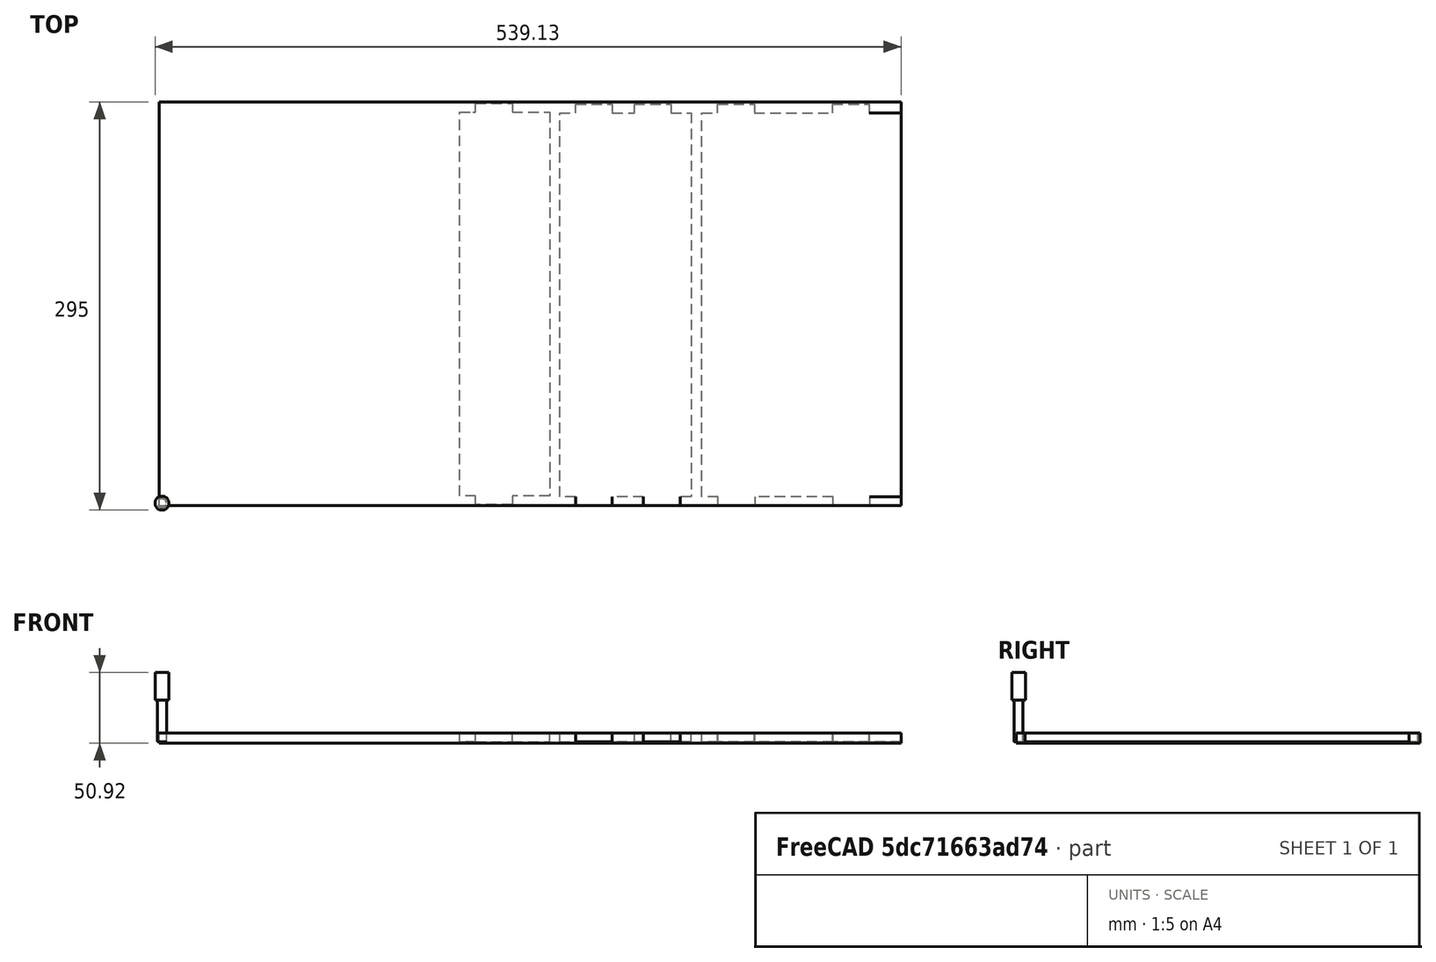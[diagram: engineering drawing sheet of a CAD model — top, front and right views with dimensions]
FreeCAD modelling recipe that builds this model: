
FCSTD DOCUMENT  (FreeCAD 0.19RUnknown)
Label: Stand3
License: All rights reserved
LicenseURL: http://en.wikipedia.org/wiki/All_rights_reserved
objects: Part::FeaturePython×7, Path::FeaturePython×5, Sketcher::SketchObject×4, PartDesign::Pad×4, PartDesign::Body×4, App::DocumentObjectGroup×2, PartDesign::Fillet×1, Spreadsheet::Sheet×1, Part::Mirroring×1, Mesh::FeaturePython×1, App::FeaturePython×1, Path::FeatureCompoundPython×1
note: 29 computed .brp shape members not serialized (recipe doc carries the construction recipe); baked Part::Feature solids carry a one-line shape summary decoded from their .brp

FEATURE [Sketcher::SketchObject] Sketch
  FullyConstrained = true
  MapMode = 5
  Support = -> [XY_Plane]
  expr: .Constraints.LowerSlotGap = <<Spreadsheet>>.TongueGapLower
  expr: Constraints[67] = <<Spreadsheet>>.Tool
  expr: Constraints[94] = <<Spreadsheet>>.SlotCentre
  expr: Constraints[83] = <<Spreadsheet>>.TongueToBack
  expr: Constraints[81] = <<Spreadsheet>>.Tool
  expr: Constraints[92] = <<Spreadsheet>>.Tool
  expr: Constraints[72] = <<Spreadsheet>>.TongueToBack
  expr: Constraints[91] = <<Spreadsheet>>.SlotSize
  expr: Constraints[71] = <<Spreadsheet>>.SlotSize
  expr: Constraints[53] = <<Spreadsheet>>.Tool
  expr: Constraints[68] = <<Spreadsheet>>.Tool
  expr: Constraints[82] = <<Spreadsheet>>.SlotSize
  expr: Constraints[52] = <<Spreadsheet>>.SlotSize
  expr: Constraints[27] = <<Spreadsheet>>.Top
  expr: Constraints[70] = <<Spreadsheet>>.SlotSize
  expr: Constraints[55] = <<Spreadsheet>>.TongueToBack
  expr: Constraints[29] = <<Spreadsheet>>.Bottom
  expr: .Constraints.MidSlotGap = <<Spreadsheet>>.TongueGapMid
  expr: Constraints[26] = <<Spreadsheet>>.Height
  expr: Constraints[107] = <<Spreadsheet>>.TongueToBack
  sketch-geometry (40):
    g0: LineSegment StartX=0 StartY=290 StartZ=0 EndX=50 EndY=290 EndZ=0
    g1: LineSegment StartX=150 StartY=0 StartZ=0 EndX=120 EndY=0 EndZ=0
    g2: LineSegment StartX=0 StartY=0 StartZ=0 EndX=0 EndY=290 EndZ=0
    g3: LineSegment StartX=50 StartY=290 StartZ=0 EndX=150 EndY=0 EndZ=0
    g4: LineSegment StartX=15 StartY=210 StartZ=0 EndX=15 EndY=130 EndZ=0
    g5: LineSegment StartX=15 StartY=130 StartZ=0 EndX=89.3057 EndY=130 EndZ=0
    g6: LineSegment StartX=89.3057 StartY=130 StartZ=0 EndX=61.7195 EndY=210 EndZ=0
    g7: LineSegment StartX=61.7195 StartY=210 StartZ=0 EndX=15 EndY=210 EndZ=0
    g8: LineSegment StartX=15 StartY=110 StartZ=0 EndX=15 EndY=33.2 EndZ=0
    g9: LineSegment StartX=15 StartY=33.2 StartZ=0 EndX=122.685 EndY=33.2 EndZ=0
    g10: LineSegment StartX=122.685 StartY=33.2 StartZ=0 EndX=96.2022 EndY=110 EndZ=0
    g11: LineSegment StartX=96.2022 StartY=110 StartZ=0 EndX=15 EndY=110 EndZ=0
    g12: LineSegment StartX=120 StartY=0 StartZ=0 EndX=120 EndY=13.2 EndZ=0
    g13: LineSegment StartX=120 StartY=13.2 StartZ=0 EndX=30 EndY=13.2 EndZ=0
    g14: LineSegment StartX=30 StartY=13.2 StartZ=0 EndX=30 EndY=0 EndZ=0
    g15: LineSegment StartX=30 StartY=0 StartZ=0 EndX=0 EndY=0 EndZ=0
    g16: ArcOfCircle CenterX=18 CenterY=220 CenterZ=0 NormalX=0 NormalY=0 NormalZ=1 AngleXU=0 Radius=3.25 StartAngle=1.5708 EndAngle=4.71239
    g17: ArcOfCircle CenterX=38 CenterY=220 CenterZ=0 NormalX=0 NormalY=0 NormalZ=1 AngleXU=0 Radius=3.25 StartAngle=4.71239 EndAngle=7.85398
    g18: LineSegment StartX=18 StartY=216.75 StartZ=0 EndX=38 EndY=216.75 EndZ=0
    g19: LineSegment StartX=38 StartY=223.25 StartZ=0 EndX=18 EndY=223.25 EndZ=0
    g20: ArcOfCircle CenterX=60.5 CenterY=120 CenterZ=0 NormalX=0 NormalY=0 NormalZ=1 AngleXU=0 Radius=3.25 StartAngle=1.5708 EndAngle=4.71239
    g21: ArcOfCircle CenterX=80.5 CenterY=120 CenterZ=0 NormalX=0 NormalY=0 NormalZ=1 AngleXU=0 Radius=3.25 StartAngle=4.71239 EndAngle=7.85398
    g22: LineSegment StartX=60.5 StartY=116.75 StartZ=0 EndX=80.5 EndY=116.75 EndZ=0
    g23: LineSegment StartX=80.5 StartY=123.25 StartZ=0 EndX=60.5 EndY=123.25 EndZ=0
    g24: ArcOfCircle CenterX=18 CenterY=120 CenterZ=0 NormalX=0 NormalY=0 NormalZ=1 AngleXU=0 Radius=3.25 StartAngle=1.5708 EndAngle=4.71239
    g25: ArcOfCircle CenterX=38 CenterY=120 CenterZ=0 NormalX=0 NormalY=0 NormalZ=1 AngleXU=0 Radius=3.25 StartAngle=4.71239 EndAngle=7.85398
    g26: LineSegment StartX=18 StartY=116.75 StartZ=0 EndX=38 EndY=116.75 EndZ=0
    g27: LineSegment StartX=38 StartY=123.25 StartZ=0 EndX=18 EndY=123.25 EndZ=0
    g28: ArcOfCircle CenterX=18 CenterY=23.2 CenterZ=0 NormalX=0 NormalY=0 NormalZ=1 AngleXU=0 Radius=3.25 StartAngle=1.5708 EndAngle=4.71239
    g29: ArcOfCircle CenterX=38 CenterY=23.2 CenterZ=0 NormalX=0 NormalY=0 NormalZ=1 AngleXU=0 Radius=3.25 StartAngle=4.71239 EndAngle=7.85398
    g30: LineSegment StartX=18 StartY=19.95 StartZ=0 EndX=38 EndY=19.95 EndZ=0
    g31: LineSegment StartX=38 StartY=26.45 StartZ=0 EndX=18 EndY=26.45 EndZ=0
    g32: ArcOfCircle CenterX=101 CenterY=23.2 CenterZ=0 NormalX=0 NormalY=0 NormalZ=1 AngleXU=0 Radius=3.25 StartAngle=1.5708 EndAngle=4.71239
    g33: ArcOfCircle CenterX=121 CenterY=23.2 CenterZ=0 NormalX=0 NormalY=0 NormalZ=1 AngleXU=0 Radius=3.25 StartAngle=4.71239 EndAngle=7.85398
    g34: LineSegment StartX=101 StartY=19.95 StartZ=0 EndX=121 EndY=19.95 EndZ=0
    g35: LineSegment StartX=121 StartY=26.45 StartZ=0 EndX=101 EndY=26.45 EndZ=0
    g36: LineSegment StartX=18 StartY=280 StartZ=0 EndX=18 EndY=230 EndZ=0
    g37: LineSegment StartX=18 StartY=230 StartZ=0 EndX=54.8229 EndY=230 EndZ=0
    g38: LineSegment StartX=54.8229 StartY=230 StartZ=0 EndX=37.5815 EndY=280 EndZ=0
    g39: LineSegment StartX=37.5815 StartY=280 StartZ=0 EndX=18 EndY=280 EndZ=0
  constraints (109):
    c: Coincident(g15,g2)
    c: Coincident(g2,g0)
    c: Horizontal(g0)
    c: Horizontal(g1)
    c: Vertical(g2)
    c: Vertical(g4)
    c: Coincident(g4,g5)
    c: Horizontal(g5)
    c: Coincident(g5,g6)
    c: Coincident(g6,g7)
    c: Coincident(g7,g4)
    c: Vertical(g8)
    c: Coincident(g8,g9)
    c: Coincident(g9,g10)
    c: Coincident(g10,g11)
    c: Coincident(g11,g8)
    c: Horizontal(g11)
    c: Coincident(g12,g13)
    c: Coincident(g13,g14)
    c: Horizontal(g13)
    c: Vertical(g12)
    c: Vertical(g14)
    c: Coincident(g15,g-1)
    c: Coincident(g0,g3)
    c: Parallel(g3,g10)
    c: Parallel(g3,g6)
    c: DistanceY(g2,g2) = 290
    c: DistanceX(g0,g0) = 50
    c: Coincident(g3,g1)
    c: DistanceX(g2,g1) = 150
    c: DistanceX(g15,g15) = 30
    c: DistanceX(g1,g1) = 30
    c: Coincident(g12,g1)
    c: Parallel(g13,g9)
    c: Parallel(g5,g7)
    c: Coincident(g14,g15)
    c: DistanceY(g14,g13) = 13.2
    c: DistanceY(g13,g8) = 20
    c: DistanceY(g8,g4) = 20
    c: DistanceY(g4,g0) = 80
    c: DistanceX(g2,g8) = 15
    c: DistanceX(g2,g4) = 15
    c: Horizontal(g15)
    c: Distance(g5,g3) = 15
    c: Distance(g10,g3) = 15
    c: DistanceY(g1,g2) = 0
    c: Tangent(g16,g18) = -1.5708
    c: Tangent(g18,g17) = -1.5708
    c: Tangent(g17,g19) = -1.5708
    c: Tangent(g19,g16) = -1.5708
    c: Equal(g16,g17)
    c: Horizontal(g18)
    c: DistanceX(g16,g17) = 20
    c: Diameter(g17) = 6.5
    c: DistanceY(g4,g16) = 10
    c: DistanceX(g0,g16) = 18
    c: Tangent(g20,g22) = -1.5708
    c: Tangent(g22,g21) = -1.5708
    c: Tangent(g21,g23) = -1.5708
    c: Tangent(g23,g20) = -1.5708
    c: Equal(g20,g21)
    c: Horizontal(g22)
    c: Tangent(g24,g26) = -1.5708
    c: Tangent(g26,g25) = -1.5708
    c: Tangent(g25,g27) = -1.5708
    c: Tangent(g27,g24) = -1.5708
    c: Equal(g24,g25)
    c: Diameter(g21) = 6.5
    c: Diameter(g24) = 6.5
    c: Parallel(g27,g5)
    c: DistanceX(g20,g21) = 20
    c: DistanceX(g24,g25) = 20
    c: DistanceX(g2,g24) = 18
    c: DistanceY(g8,g24) = 10
    c: DistanceY(g10,g21) = 10
    c: Tangent(g28,g30) = -1.5708
    c: Tangent(g30,g29) = -1.5708
    c: Tangent(g29,g31) = -1.5708
    c: Tangent(g31,g28) = -1.5708
    c: Equal(g28,g29)
    c: Horizontal(g30)
    c: Diameter(g29) = 6.5
    c: DistanceX(g28,g29) = 20
    c: DistanceX(g2,g28) = 18
    c: DistanceY(g13,g28) = 10
    c: Tangent(g32,g34) = -1.5708
    c: Tangent(g34,g33) = -1.5708
    c: Tangent(g33,g35) = -1.5708
    c: Tangent(g35,g32) = -1.5708
    c: Equal(g32,g33)
    c: Horizontal(g34)
    c: DistanceX(g32,g33) = 20
    c: Diameter(g33) = 6.5
    c: DistanceY(g12,g33) = 10
    c: DistanceY(g2,g24) = 120
    c: DistanceX(g25,g20) = 22.5  'MidSlotGap'
    c: DistanceX(g29,g32) = 63  'LowerSlotGap'
    c: Vertical(g36)
    c: Coincident(g36,g37)
    c: Horizontal(g37)
    c: Coincident(g37,g38)
    c: Coincident(g38,g39)
    c: Coincident(g39,g36)
    c: Horizontal(g39)
    c: DistanceY(g16,g36) = 10
    c: DistanceY(g36,g0) = 10
    c: Parallel(g38,g3)
    c: DistanceX(g0,g36) = 18
    c: Distance(g37,g3) = 15
FEATURE [PartDesign::Pad] Pad
  Direction = (0,0,1)
  Length = 6.25
  Length2 = 100
  Profile = -> Sketch
  Type = 0
  expr: Length = <<Spreadsheet>>.Thickness
FEATURE [PartDesign::Fillet] Fillet
  Base = -> Pad [Edge20,Edge2,Edge1,Edge5,Edge8,Edge17,Edge44,Edge37,Edge32,Edge25,Edge38,Edge26,Edge29,Edge41,Edge14,Edge11,Edge49,Edge50,Edge56,Edge53]
  BaseFeature = -> Pad
  Radius = 6.5
  SupportTransform = false
  expr: Radius = <<Spreadsheet>>.Tool
FEATURE [PartDesign::Body] Body
  Group = -> [Sketch,Pad,Fillet]
  Origin = -> Origin
  Placement = pos=(-2,0,0) rot=(0,0,1;0rad)
  Tip = -> Fillet
FEATURE [Spreadsheet::Sheet] Spreadsheet
  cells = A2=Material Thickness; B2(Thickness)=6.25; A3=Tool Size; B3(Tool)=6.5; A5=Height; B5(Height)=290; A6=Bottom Width; B6(Bottom)=150; A7=Top Width; B7(Top)=50; A8=SlotSize; B8(SlotSize)=20; A9=TongueSize; B9(TongueSize)==B8 + B3; A10=Tongue to back; B10(TongueToBack)=18; A11=Centre; B11(SlotCentre)=120; A12=Mid Tongue Gap; B12(TongueGapMid)=22.5; A13=Lower Tongue Gap; B13(TongueGapLower)=63; A15=TopShelf; B15(ShelfTop)=65; A16=MidShelf; B16(ShelfMid)==(B6 + B7) / 2 - 5; A17=Bottom Shelf; B17(ShelfBottom)==B6 - 6; A18=Shelf Width; B18(ShelfWidth)==B5 - B2 * 2
FEATURE [Part::Mirroring] mirror  label="Body (mirrored) "
  Base = (159.181,124.226,5.79083)
  Normal = (-0.999887,-0.00161748,0.0149187)
  Placement = pos=(-113.202,287.893,10.586) rot=(0.99989,0.002927,-0.014571;3.14394rad)
  Source = -> Body
FEATURE [Sketcher::SketchObject] Sketch001
  FullyConstrained = false
  MapMode = 5
  Support = -> [XY_Plane001]
  expr: Constraints[34] = <<Spreadsheet>>.ShelfWidth
  expr: Constraints[30] = <<Spreadsheet>>.TongueToBack - <<Spreadsheet>>.Tool
  expr: Constraints[9] = <<Spreadsheet>>.ShelfWidth
  expr: Constraints[27] = <<Spreadsheet>>.Thickness
  expr: Constraints[29] = <<Spreadsheet>>.TongueToBack - <<Spreadsheet>>.Tool
  expr: Constraints[26] = <<Spreadsheet>>.TongueSize
  expr: Constraints[8] = <<Spreadsheet>>.ShelfTop
  expr: Constraints[16] = <<Spreadsheet>>.Thickness
  expr: Constraints[15] = <<Spreadsheet>>.TongueSize
  sketch-geometry (13):
    g0: LineSegment StartX=222.154 StartY=283.723 StartZ=0 EndX=231.81 EndY=283.723 EndZ=0
    g1: LineSegment StartX=287.154 StartY=283.75 StartZ=0 EndX=287.154 EndY=6.25 EndZ=0
    g2: LineSegment StartX=287.154 StartY=6.25 StartZ=0 EndX=260.154 EndY=6.25 EndZ=0
    g3: LineSegment StartX=222.154 StartY=6.22299 StartZ=0 EndX=222.154 EndY=283.723 EndZ=0
    g4: LineSegment StartX=260.154 StartY=6.25 StartZ=0 EndX=260.154 EndY=0 EndZ=0
    g5: LineSegment StartX=260.154 StartY=0 StartZ=0 EndX=233.654 EndY=0 EndZ=0
    g6: LineSegment StartX=233.654 StartY=0 StartZ=0 EndX=233.654 EndY=6.22299 EndZ=0
    g7: LineSegment StartX=233.654 StartY=6.22299 StartZ=0 EndX=222.154 EndY=6.22299 EndZ=0
    g8: LineSegment StartX=233.654 StartY=290 StartZ=0 EndX=260.154 EndY=290 EndZ=0
    g9: LineSegment StartX=260.154 StartY=290 StartZ=0 EndX=260.154 EndY=283.75 EndZ=0
    g10: LineSegment StartX=231.81 StartY=283.723 StartZ=0 EndX=233.654 EndY=283.723 EndZ=0
    g11: LineSegment StartX=233.654 StartY=283.723 StartZ=0 EndX=233.654 EndY=290 EndZ=0
    g12: LineSegment StartX=260.154 StartY=283.75 StartZ=0 EndX=287.154 EndY=283.75 EndZ=0
  constraints (36):
    c: Coincident(g12,g1)
    c: Coincident(g1,g2)
    c: Coincident(g7,g3)
    c: Coincident(g3,g0)
    c: Horizontal(g0)
    c: Horizontal(g2)
    c: Vertical(g1)
    c: Vertical(g3)
    c: DistanceX(g0,g12) = 65
    c: DistanceY(g3,g3) = 277.5
    c: Coincident(g4,g5)
    c: Coincident(g5,g6)
    c: Horizontal(g5)
    c: Vertical(g4)
    c: Vertical(g6)
    c: DistanceX(g5,g5) = 26.5
    c: DistanceY(g4,g4) = 6.25
    c: DistanceY(g-1,g5) = 0
    c: Parallel(g5,g7)
    c: Coincident(g8,g9)
    c: Coincident(g10,g11)
    c: Coincident(g11,g8)
    c: Horizontal(g8)
    c: Horizontal(g10)
    c: Vertical(g9)
    c: Vertical(g11)
    c: DistanceX(g8,g8) = 26.5
    c: DistanceY(g9,g9) = 6.25
    c: PointOnObject(g10,g0)
    c: DistanceX(g0,g8) = 11.5
    c: DistanceX(g3,g5) = 11.5
    c: Coincident(g7,g6)
    c: Coincident(g12,g9)
    c: Coincident(g2,g4)
    c: DistanceY(g1,g1) = 277.5
    c: Parallel(g12,g8)
FEATURE [PartDesign::Pad] Pad001
  Direction = (0,0,1)
  Length = 6.25
  Length2 = 10
  Profile = -> Sketch001
  Type = 0
  expr: Length = <<Spreadsheet>>.Thickness
FEATURE [PartDesign::Body] Body001  label="TopShelf"
  Group = -> [Sketch001,Pad001]
  Origin = -> Origin001
  Placement = pos=(-7,-1,0) rot=(0,0,1;0rad)
  Tip = -> Pad001
FEATURE [Sketcher::SketchObject] Sketch002
  FullyConstrained = false
  MapMode = 5
  Support = -> [XY_Plane002]
  expr: Constraints[9] = <<Spreadsheet>>.ShelfMid
  expr: Constraints[57] = <<Spreadsheet>>.ShelfWidth
  expr: Constraints[55] = <<Spreadsheet>>.Thickness
  expr: Constraints[54] = <<Spreadsheet>>.Thickness
  expr: Constraints[8] = <<Spreadsheet>>.ShelfWidth
  expr: Constraints[56] = <<Spreadsheet>>.Thickness
  expr: Constraints[48] = <<Spreadsheet>>.Thickness
  expr: Constraints[47] = <<Spreadsheet>>.Thickness
  expr: Constraints[46] = <<Spreadsheet>>.Thickness
  expr: Constraints[42] = <<Spreadsheet>>.TongueGapMid
  expr: Constraints[37] = <<Spreadsheet>>.TongueToBack - <<Spreadsheet>>.Tool
  expr: Constraints[43] = <<Spreadsheet>>.TongueSize
  expr: Constraints[36] = <<Spreadsheet>>.TongueSize
  expr: Constraints[58] = <<Spreadsheet>>.Thickness
  expr: Constraints[49] = <<Spreadsheet>>.Thickness
  expr: Constraints[33] = <<Spreadsheet>>.TongueSize
  expr: Constraints[38] = <<Spreadsheet>>.TongueSize
  expr: Constraints[32] = <<Spreadsheet>>.TongueGapMid - <<Spreadsheet>>.Tool
  expr: Constraints[31] = <<Spreadsheet>>.TongueToBack - <<Spreadsheet>>.Tool
  sketch-geometry (20):
    g0: LineSegment StartX=280.428 StartY=276.137 StartZ=0 EndX=291.928 EndY=276.137 EndZ=0
    g1: LineSegment StartX=375.428 StartY=276.137 StartZ=0 EndX=375.428 EndY=-1.36323 EndZ=0
    g2: LineSegment StartX=375.428 StartY=-1.36323 StartZ=0 EndX=367.428 EndY=-1.36323 EndZ=0
    g3: LineSegment StartX=280.428 StartY=-1.36323 StartZ=0 EndX=280.428 EndY=276.137 EndZ=0
    g4: LineSegment StartX=291.928 StartY=282.387 StartZ=0 EndX=318.428 EndY=282.387 EndZ=0
    g5: LineSegment StartX=318.428 StartY=282.387 StartZ=0 EndX=318.428 EndY=276.137 EndZ=0
    g6: LineSegment StartX=291.928 StartY=276.137 StartZ=0 EndX=291.928 EndY=282.387 EndZ=0
    g7: LineSegment StartX=334.428 StartY=282.387 StartZ=0 EndX=360.928 EndY=282.387 EndZ=0
    g8: LineSegment StartX=360.928 StartY=282.387 StartZ=0 EndX=360.928 EndY=276.137 EndZ=0
    g9: LineSegment StartX=334.428 StartY=276.137 StartZ=0 EndX=334.428 EndY=282.387 EndZ=0
    g10: LineSegment StartX=318.428 StartY=-1.36323 StartZ=0 EndX=318.428 EndY=-7.61323 EndZ=0
    g11: LineSegment StartX=318.428 StartY=-7.61323 StartZ=0 EndX=291.928 EndY=-7.61323 EndZ=0
    g12: LineSegment StartX=291.928 StartY=-7.61323 StartZ=0 EndX=291.928 EndY=-1.36323 EndZ=0
    g13: LineSegment StartX=367.428 StartY=-1.36323 StartZ=0 EndX=367.428 EndY=-7.61323 EndZ=0
    g14: LineSegment StartX=367.428 StartY=-7.61323 StartZ=0 EndX=340.928 EndY=-7.61323 EndZ=0
    g15: LineSegment StartX=340.928 StartY=-7.61323 StartZ=0 EndX=340.928 EndY=-1.36323 EndZ=0
    g16: LineSegment StartX=318.428 StartY=276.137 StartZ=0 EndX=334.428 EndY=276.137 EndZ=0
    g17: LineSegment StartX=360.928 StartY=276.137 StartZ=0 EndX=375.428 EndY=276.137 EndZ=0
    g18: LineSegment StartX=291.928 StartY=-1.36323 StartZ=0 EndX=280.428 EndY=-1.36323 EndZ=0
    g19: LineSegment StartX=340.928 StartY=-1.36323 StartZ=0 EndX=318.428 EndY=-1.36323 EndZ=0
  constraints (59):
    c: Coincident(g17,g1)
    c: Coincident(g1,g2)
    c: Coincident(g18,g3)
    c: Coincident(g3,g0)
    c: Horizontal(g0)
    c: Horizontal(g2)
    c: Vertical(g1)
    c: Vertical(g3)
    c: DistanceY(g1,g1) = 277.5
    c: DistanceX(g0,g17) = 95
    c: Coincident(g4,g5)
    c: Coincident(g6,g4)
    c: Horizontal(g4)
    c: Vertical(g5)
    c: Vertical(g6)
    c: Coincident(g7,g8)
    c: Coincident(g9,g7)
    c: Horizontal(g7)
    c: Vertical(g8)
    c: Vertical(g9)
    c: PointOnObject(g8,g0)
    c: Coincident(g10,g11)
    c: Coincident(g11,g12)
    c: Horizontal(g11)
    c: Vertical(g10)
    c: Vertical(g12)
    c: Coincident(g13,g14)
    c: Coincident(g14,g15)
    c: Horizontal(g14)
    c: Vertical(g13)
    c: Vertical(g15)
    c: DistanceX(g0,g4) = 11.5
    c: DistanceX(g4,g7) = 16
    c: DistanceX(g4,g4) = 26.5
    c: Coincident(g16,g5)
    c: PointOnObject(g16,g9)
    c: DistanceX(g7,g7) = 26.5
    c: DistanceX(g3,g11) = 11.5
    c: DistanceX(g11,g11) = 26.5
    c: Coincident(g18,g12)
    c: Coincident(g10,g19)
    c: Coincident(g19,g15)
    c: DistanceX(g19,g19) = 22.5
    c: DistanceX(g14,g14) = 26.5
    c: Coincident(g0,g6)
    c: Coincident(g17,g8)
    c: DistanceY(g1,g7) = 6.25
    c: DistanceY(g9,g9) = 6.25
    c: DistanceY(g5,g5) = 6.25
    c: DistanceY(g6,g6) = 6.25
    c: Parallel(g16,g4)
    c: Parallel(g18,g11)
    c: Parallel(g19,g11)
    c: Coincident(g2,g13)
    c: DistanceY(g12,g12) = 6.25
    c: DistanceY(g15,g15) = 6.25
    c: DistanceY(g13,g13) = 6.25
    c: DistanceY(g3,g3) = 277.5
    c: DistanceY(g10,g10) = 6.25
FEATURE [PartDesign::Pad] Pad002
  Direction = (0,0,1)
  Length = 6.25
  Length2 = 10
  Profile = -> Sketch002
  Type = 0
  expr: Length = <<Spreadsheet>>.Thickness
FEATURE [PartDesign::Body] Body002  label="MidShelf"
  Group = -> [Sketch002,Pad002]
  Origin = -> Origin002
  Placement = pos=(7,6,0) rot=(0,0,1;0rad)
  Tip = -> Pad002
FEATURE [Sketcher::SketchObject] Sketch003
  FullyConstrained = false
  MapMode = 5
  Support = -> [XY_Plane003]
  expr: Constraints[57] = <<Spreadsheet>>.Thickness
  expr: Constraints[55] = <<Spreadsheet>>.ShelfWidth
  expr: Constraints[54] = <<Spreadsheet>>.TongueToBack - <<Spreadsheet>>.Thickness
  expr: Constraints[53] = <<Spreadsheet>>.TongueGapLower - <<Spreadsheet>>.Tool
  expr: Constraints[51] = <<Spreadsheet>>.TongueSize
  expr: Constraints[4] = <<Spreadsheet>>.ShelfBottom
  expr: Constraints[46] = <<Spreadsheet>>.Thickness
  expr: Constraints[45] = <<Spreadsheet>>.Thickness
  expr: Constraints[49] = <<Spreadsheet>>.Thickness
  expr: Constraints[56] = <<Spreadsheet>>.Thickness
  expr: Constraints[44] = <<Spreadsheet>>.Thickness
  expr: Constraints[52] = <<Spreadsheet>>.TongueSize
  expr: Constraints[48] = <<Spreadsheet>>.ShelfWidth
  expr: Constraints[37] = <<Spreadsheet>>.TongueToBack - <<Spreadsheet>>.Tool
  expr: Constraints[35] = <<Spreadsheet>>.TongueSize
  expr: Constraints[34] = <<Spreadsheet>>.TongueSize
  expr: Constraints[36] = <<Spreadsheet>>.TongueGapLower - <<Spreadsheet>>.Tool
  expr: Constraints[50] = <<Spreadsheet>>.Thickness
  sketch-geometry (20):
    g0: LineSegment StartX=533.13 StartY=286.184 StartZ=0 EndX=533.13 EndY=8.68426 EndZ=0
    g1: LineSegment StartX=533.13 StartY=8.68426 StartZ=0 EndX=510.38 EndY=8.68426 EndZ=0
    g2: LineSegment StartX=389.13 StartY=8.68426 StartZ=0 EndX=389.13 EndY=286.184 EndZ=0
    g3: LineSegment StartX=400.63 StartY=292.434 StartZ=0 EndX=427.13 EndY=292.434 EndZ=0
    g4: LineSegment StartX=427.13 StartY=292.434 StartZ=0 EndX=427.13 EndY=286.184 EndZ=0
    g5: LineSegment StartX=400.63 StartY=286.184 StartZ=0 EndX=400.63 EndY=292.434 EndZ=0
    g6: LineSegment StartX=483.63 StartY=292.434 StartZ=0 EndX=510.13 EndY=292.434 EndZ=0
    g7: LineSegment StartX=510.13 StartY=292.434 StartZ=0 EndX=510.13 EndY=286.184 EndZ=0
    g8: LineSegment StartX=483.63 StartY=286.184 StartZ=0 EndX=483.63 EndY=292.434 EndZ=0
    g9: LineSegment StartX=427.38 StartY=8.68426 StartZ=0 EndX=427.38 EndY=2.43426 EndZ=0
    g10: LineSegment StartX=427.38 StartY=2.43426 StartZ=0 EndX=400.88 EndY=2.43426 EndZ=0
    g11: LineSegment StartX=400.88 StartY=2.43426 StartZ=0 EndX=400.88 EndY=8.68426 EndZ=0
    g12: LineSegment StartX=510.38 StartY=8.68426 StartZ=0 EndX=510.38 EndY=2.43426 EndZ=0
    g13: LineSegment StartX=510.38 StartY=2.43426 StartZ=0 EndX=483.88 EndY=2.43426 EndZ=0
    g14: LineSegment StartX=483.88 StartY=2.43426 StartZ=0 EndX=483.88 EndY=8.68426 EndZ=0
    g15: LineSegment StartX=389.13 StartY=286.184 StartZ=0 EndX=400.63 EndY=286.184 EndZ=0
    g16: LineSegment StartX=427.13 StartY=286.184 StartZ=0 EndX=483.63 EndY=286.184 EndZ=0
    g17: LineSegment StartX=510.13 StartY=286.184 StartZ=0 EndX=533.13 EndY=286.184 EndZ=0
    g18: LineSegment StartX=400.88 StartY=8.68426 StartZ=0 EndX=389.13 EndY=8.68426 EndZ=0
    g19: LineSegment StartX=483.88 StartY=8.68426 StartZ=0 EndX=427.38 EndY=8.68426 EndZ=0
  constraints (58):
    c: Coincident(g0,g1)
    c: Coincident(g18,g2)
    c: Horizontal(g1)
    c: Vertical(g0)
    c: DistanceX(g2,g0) = 144
    c: Coincident(g3,g4)
    c: Coincident(g5,g3)
    c: Horizontal(g3)
    c: Vertical(g4)
    c: Vertical(g5)
    c: Coincident(g6,g7)
    c: Coincident(g8,g6)
    c: Horizontal(g6)
    c: Vertical(g7)
    c: Vertical(g8)
    c: Coincident(g9,g10)
    c: Coincident(g10,g11)
    c: Horizontal(g10)
    c: Vertical(g9)
    c: Vertical(g11)
    c: Coincident(g12,g13)
    c: Coincident(g13,g14)
    c: Horizontal(g13)
    c: Vertical(g12)
    c: Vertical(g14)
    c: Horizontal(g17)
    c: Coincident(g7,g17)
    c: Coincident(g17,g0)
    c: Coincident(g8,g16)
    c: Coincident(g16,g4)
    c: Coincident(g15,g5)
    c: Coincident(g2,g15)
    c: Parallel(g15,g3)
    c: Parallel(g16,g3)
    c: DistanceX(g3,g3) = 26.5
    c: DistanceX(g6,g6) = 26.5
    c: DistanceX(g3,g6) = 56.5
    c: DistanceX(g2,g3) = 11.5
    c: Coincident(g18,g11)
    c: Coincident(g9,g19)
    c: Coincident(g19,g14)
    c: Coincident(g12,g1)
    c: Parallel(g18,g10)
    c: Parallel(g10,g19)
    c: DistanceY(g11,g11) = 6.25
    c: DistanceY(g9,g9) = 6.25
    c: DistanceY(g14,g14) = 6.25
    c: Perpendicular(g18,g2)
    c: DistanceY(g2,g2) = 277.5
    c: DistanceY(g5,g5) = 6.25
    c: DistanceY(g8,g8) = 6.25
    c: DistanceX(g10,g10) = 26.5
    c: DistanceX(g13,g13) = 26.5
    c: DistanceX(g19,g19) = 56.5
    c: DistanceX(g18,g18) = 11.75
    c: DistanceY(g0,g0) = 277.5
    c: DistanceY(g12,g12) = 6.25
    c: DistanceY(g7,g7) = 6.25
FEATURE [PartDesign::Pad] Pad003
  Direction = (0,0,1)
  Length = 6.25
  Length2 = 10
  Profile = -> Sketch003
  Type = 0
  expr: Length = <<Spreadsheet>>.Thickness
FEATURE [PartDesign::Body] Body003  label="BottomShelf"
  Group = -> [Sketch003,Pad003]
  Origin = -> Origin003
  Placement = pos=(1,-4,0) rot=(0,0,1;0rad)
  Tip = -> Pad003
FEATURE [Mesh::FeaturePython] CutMaterial001  # WARN: FeaturePython — macro-defined, semantics opaque (R4)
FEATURE [App::FeaturePython] SetupSheet  # Path/CAM operation (typed FeaturePython)
  ClearanceHeightExpression = OpStockZMax+SetupSheet.ClearanceHeightOffset
  ClearanceHeightOffset = 5
  CoolantMode = 0
  CoolantModes = None | Flood | Mist
  FinalDepthExpression = OpFinalDepth
  HorizRapid = 0
  SafeHeightExpression = OpStockZMax+SetupSheet.SafeHeightOffset
  SafeHeightOffset = 3
  StartDepthExpression = OpStartDepth
  StepDownExpression = OpToolDiameter
  VertRapid = 0
FEATURE [Part::FeaturePython] Clone  label="Model-Body"  # Draft clone (typed FeaturePython)
  AttacherType = Attacher::AttachEngine3D
  Fuse = false
  Objects = -> [Body]
  PathResource = Model
  Placement = pos=(-2,0,0) rot=(0,0,1;0rad)
  Scale = (1,1,1)
FEATURE [Part::FeaturePython] Clone001  label="Model-Body (mirrored) "  # Draft clone (typed FeaturePython)
  AttacherType = Attacher::AttachEngine3D
  Fuse = false
  Objects = -> [mirror]
  PathResource = Model
  Placement = pos=(-113.202,287.893,10.586) rot=(0.99989,0.002927,-0.014571;3.14394rad)
  Scale = (1,1,1)
FEATURE [Part::FeaturePython] Clone002  label="Model-BottomShelf"  # Draft clone (typed FeaturePython)
  AttacherType = Attacher::AttachEngine3D
  Fuse = false
  Objects = -> [Body003]
  PathResource = Model
  Placement = pos=(1,-4,0) rot=(0,0,1;0rad)
  Scale = (1,1,1)
FEATURE [Part::FeaturePython] Clone003  label="Model-MidShelf"  # Draft clone (typed FeaturePython)
  AttacherType = Attacher::AttachEngine3D
  Fuse = false
  Objects = -> [Body002]
  PathResource = Model
  Placement = pos=(7,6,0) rot=(0,0,1;0rad)
  Scale = (1,1,1)
FEATURE [Part::FeaturePython] Clone004  label="Model-TopShelf"  # Draft clone (typed FeaturePython)
  AttacherType = Attacher::AttachEngine3D
  Fuse = false
  Objects = -> [Body001]
  PathResource = Model
  Placement = pos=(-7,-1,0) rot=(0,0,1;0rad)
  Scale = (1,1,1)
FEATURE [App::DocumentObjectGroup] Model
  Group = -> [Clone,Clone001,Clone002,Clone003,Clone004]
FEATURE [Part::FeaturePython] Stock001  # WARN: FeaturePython — macro-defined, semantics opaque (R4)
  Height = 7.17
  Length = 536.13
  Placement = pos=(-2,-1.61323,-0.917831) rot=(0,0,1;0rad)
  StockType = CreateBox
  Width = 291.61
FEATURE [Part::FeaturePython] ToolBit001  label="6.4mm Endmill"  # Path/CAM toolbit (typed FeaturePython)
  BitPropertyNames = Chipload | CuttingEdgeHeight | Diameter | Flutes | Length | Material | ShankDiameter
  BitShape = <path>
  Chipload = 0
  CuttingEdgeHeight = 30
  Diameter = 6.4
  File = <userpath>/MensShed/CNCRouter/FreeCAD/Bit/6.4mm_Endmill.fctb
  Flutes = 0
  Length = 50
  Material = 0
  ShankDiameter = 10
  ShapeName = endmill
FEATURE [Path::FeaturePython] __4mm_Endmill  label="6.4mm Endmill001"  # Path/CAM operation (typed FeaturePython)
  HorizFeed = 20
  HorizRapid = 0
  SpindleDir = 0
  SpindleSpeed = 10000
  Tool = -> ToolBit001
  ToolNumber = 2
  VertFeed = 20
  VertRapid = 0
  expr: VertRapid = SetupSheet.VertRapid
  expr: HorizRapid = SetupSheet.HorizRapid
FEATURE [App::DocumentObjectGroup] Tools
  Group = -> [__4mm_Endmill]
FEATURE [Path::FeaturePython] Profile  label="BaseInner"  # Path/CAM operation (typed FeaturePython)
  Active = true
  AreaParams:
    Tolerance = 1e-07
    FitArcs = True
    Simplify = False
    CleanDistance = 0.0
    Accuracy = 0.01
    Unit = 1.0
    MinArcPoints = 4
    MaxArcPoints = 100
    ClipperScale = 10000000.0
    Fill = 0
    Coplanar = 0
    Reorient = True
    Outline = False
    Explode = False
    OpenMode = 0
    Deflection = 0.01
    SubjectFill = 0
    ClipFill = 0
    Offset = -3.2
    ExtraPass = 0
    Stepover = 0.0
    LastStepover = 0.0
    JoinType = 0
    EndType = 0
    MiterLimit = 2.0
    RoundPrecision = 0.0
    PocketMode = 0
    ToolRadius = 1.0
    PocketExtraOffset = 0.0
    PocketStepover = 0.0
    PocketLastStepover = 0.0
    FromCenter = False
    Angle = 45.0
    AngleShift = 0.0
    Shift = 0.0
    Thicken = False
    SectionCount = -1
    Stepdown = 1.0
    SectionOffset = 0.0
    SectionTolerance = 1e-06
    SectionMode = 2
    Project = False
  AttemptInverseAngle = true
  Base = -> [Clone]
  ClearanceHeight = 11.2522
  CoolantMode = 0
  CycleTime = 00:02:37
  Direction = 0
  EnableRotation = 0
  FinalDepth = 0
  HandleMultipleFeatures = 0
  InverseAngle = false
  JoinType = 0
  LimitDepthToFace = true
  MiterLimit = 0.1
  OffsetExtra = 0
  OpFinalDepth = 6.25
  OpStartDepth = 6.25217
  OpStockZMax = 6.25217
  OpStockZMin = -0.917831
  OpToolDiameter = 6.4
  PathParams = {'orientation': 1, 'feedrate': 20.0, 'feedrate_v': 20.0, 'verbose': True, 'resume_height': 9.252168804445907, 'retraction': 11.252168804445907, 'return_end': True, 'preamble': False, 'start': Vector (35.94446203733697, 219.93383827467227, 11.252168804445907)}
  ReverseDirection = false
  SafeHeight = 9.25217
  Side = 1
  SplitArcs = false
  StartDepth = 6.25
  StartPoint = (0,0,0)
  StepDown = 3
  ToolController = -> __4mm_Endmill
  UseComp = true
  UseStartPoint = false
  processCircles = false
  processHoles = false
  processPerimeter = true
  expr: StepDown = 3
  expr: StartDepth = <<Spreadsheet>>.Thickness
  expr: SafeHeight = OpStockZMax + SetupSheet.SafeHeightOffset
  expr: FinalDepth = 0
  expr: ClearanceHeight = OpStockZMax + SetupSheet.ClearanceHeightOffset
FEATURE [Path::FeaturePython] Profile001  label="MirrorInner"  # Path/CAM operation (typed FeaturePython)
  Active = true
  AreaParams:
    Tolerance = 1e-07
    FitArcs = True
    Simplify = False
    CleanDistance = 0.0
    Accuracy = 0.01
    Unit = 1.0
    MinArcPoints = 4
    MaxArcPoints = 100
    ClipperScale = 10000000.0
    Fill = 0
    Coplanar = 0
    Reorient = True
    Outline = False
    Explode = False
    OpenMode = 0
    Deflection = 0.01
    SubjectFill = 0
    ClipFill = 0
    Offset = -3.2
    ExtraPass = 0
    Stepover = 0.0
    LastStepover = 0.0
    JoinType = 0
    EndType = 0
    MiterLimit = 2.0
    RoundPrecision = 0.0
    PocketMode = 0
    ToolRadius = 1.0
    PocketExtraOffset = 0.0
    PocketStepover = 0.0
    PocketLastStepover = 0.0
    FromCenter = False
    Angle = 45.0
    AngleShift = 0.0
    Shift = 0.0
    Thicken = False
    SectionCount = -1
    Stepdown = 1.0
    SectionOffset = 0.0
    SectionTolerance = 1e-06
    SectionMode = 2
    Project = False
  AttemptInverseAngle = true
  Base = -> [Clone001]
  ClearanceHeight = 11.2522
  CoolantMode = 0
  CycleTime = 00:02:44
  Direction = 0
  EnableRotation = 0
  FinalDepth = 0
  HandleMultipleFeatures = 0
  InverseAngle = false
  JoinType = 0
  LimitDepthToFace = true
  MiterLimit = 0.1
  OffsetExtra = 0
  OpFinalDepth = 5.98356
  OpStartDepth = 6.25217
  OpStockZMax = 6.25217
  OpStockZMin = -0.917831
  OpToolDiameter = 6.4
  PathParams = {'orientation': 1, 'feedrate': 20.0, 'feedrate_v': 20.0, 'verbose': True, 'resume_height': 9.252168804445907, 'retraction': 11.252168804445907, 'return_end': True, 'preamble': False, 'start': Vector (169.37301289846027, 265.90976092435335, 11.252168804445907)}
  ReverseDirection = false
  SafeHeight = 9.25217
  Side = 1
  SplitArcs = false
  StartDepth = 6.25
  StartPoint = (0,0,0)
  StepDown = 3
  ToolController = -> __4mm_Endmill
  UseComp = true
  UseStartPoint = false
  processCircles = false
  processHoles = false
  processPerimeter = true
  expr: StepDown = 3
  expr: StartDepth = <<Spreadsheet>>.Thickness
  expr: SafeHeight = OpStockZMax + SetupSheet.SafeHeightOffset
  expr: FinalDepth = 0
  expr: ClearanceHeight = OpStockZMax + SetupSheet.ClearanceHeightOffset
FEATURE [Path::FeaturePython] Profile002  # Path/CAM operation (typed FeaturePython)
  Active = true
  AreaParams:
    Tolerance = 1e-07
    FitArcs = True
    Simplify = False
    CleanDistance = 0.0
    Accuracy = 0.01
    Unit = 1.0
    MinArcPoints = 4
    MaxArcPoints = 100
    ClipperScale = 10000000.0
    Fill = 0
    Coplanar = 0
    Reorient = True
    Outline = False
    Explode = False
    OpenMode = 0
    Deflection = 0.01
    SubjectFill = 0
    ClipFill = 0
    Offset = 3.2
    ExtraPass = 0
    Stepover = 0.0
    LastStepover = 0.0
    JoinType = 0
    EndType = 0
    MiterLimit = 2.0
    RoundPrecision = 0.0
    PocketMode = 0
    ToolRadius = 1.0
    PocketExtraOffset = 0.0
    PocketStepover = 0.0
    PocketLastStepover = 0.0
    FromCenter = False
    Angle = 45.0
    AngleShift = 0.0
    Shift = 0.0
    Thicken = False
    SectionCount = -1
    Stepdown = 1.0
    SectionOffset = 0.0
    SectionTolerance = 1e-06
    SectionMode = 2
    Project = False
  AttemptInverseAngle = true
  ClearanceHeight = 11.2522
  CoolantMode = 0
  CycleTime = 00:10:25
  Direction = 0
  EnableRotation = 0
  FinalDepth = 0
  HandleMultipleFeatures = 0
  InverseAngle = false
  JoinType = 0
  LimitDepthToFace = true
  MiterLimit = 0.1
  OffsetExtra = 0
  OpFinalDepth = -0.917831
  OpStartDepth = 6.25217
  OpStockZMax = 6.25217
  OpStockZMin = -0.917831
  OpToolDiameter = 6.4
  PathParams = {'orientation': 1, 'feedrate': 20.0, 'feedrate_v': 20.0, 'verbose': True, 'resume_height': 9.252168804445907, 'retraction': 11.252168804445907, 'return_end': True, 'preamble': False, 'start': Vector (284.2281969287442, 263.5958328543131, 11.252168804445907)}
  ReverseDirection = false
  SafeHeight = 9.25217
  Side = 0
  SplitArcs = false
  StartDepth = 6.25
  StartPoint = (0,0,0)
  StepDown = 3
  ToolController = -> __4mm_Endmill
  UseComp = true
  UseStartPoint = false
  processCircles = false
  processHoles = false
  processPerimeter = true
  expr: StepDown = 3
  expr: StartDepth = <<Spreadsheet>>.Thickness
  expr: SafeHeight = OpStockZMax + SetupSheet.SafeHeightOffset
  expr: FinalDepth = 0
  expr: ClearanceHeight = OpStockZMax + SetupSheet.ClearanceHeightOffset
FEATURE [Path::FeatureCompoundPython] Operations  # Path/CAM operation (typed FeaturePython)
  Group = -> [Profile,Profile001,Profile002]
  UsePlacements = false
FEATURE [Path::FeaturePython] Job  # Path/CAM operation (typed FeaturePython)
  CycleTime = 00:15:46
  Fixtures = G54
  GeometryTolerance = 0.01
  JobType = 0
  Model = -> Model
  Operations = -> Operations
  OrderOutputBy = 0
  PostProcessor = 7
  PostProcessorOutputFile = %D/%d.ngc
  SetupSheet = -> SetupSheet
  SplitOutput = false
  Stock = -> Stock001
  Tools = -> Tools
note: 1 file-system path scrubbed to <path> (originals preserved in the JSON sidecar)
